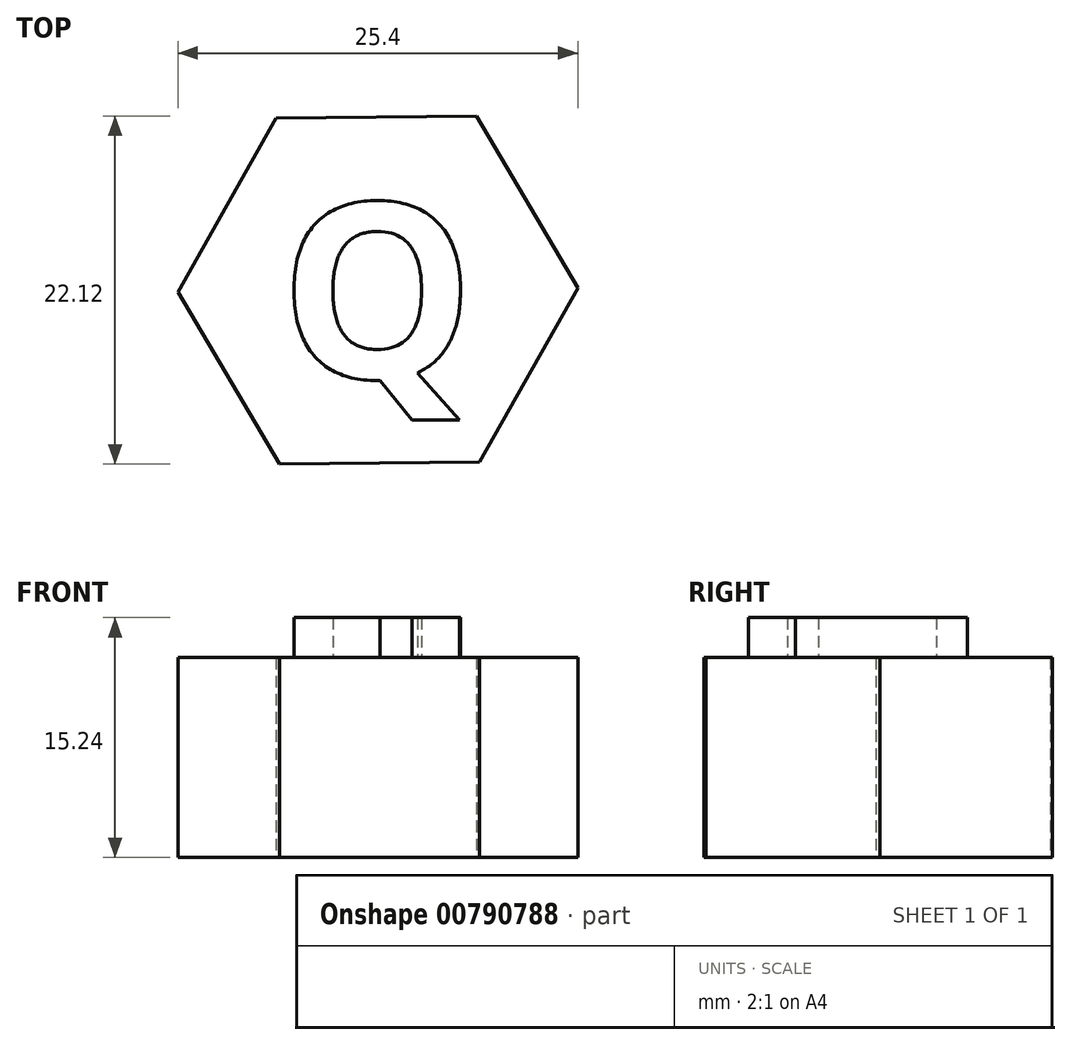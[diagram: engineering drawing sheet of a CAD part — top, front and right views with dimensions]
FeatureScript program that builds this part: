
annotation { "Feature Type Name" : "Feature", "Feature Type Description" : "" }
export const myFeature = defineFeature(function(context is Context, id is Id, definition is map)
    precondition{}
    {
        {
            var Q0;
            Q0=qCreatedBy(makeId("Top.planeOp"),FACE);
            var sketch = newSketch(context, id + "F0", { "sketchPlane" : qUnion([Q0])});
            skCircle(sketch, "E0.cCircle", {"center": v(0, 0) * mm, "radius": 11 * mm, "construction": true});
            skLineSegment(sketch, "E0.0", {"start": v(6.24, 11.06) * mm, "end": v(12.7, 0.13) * mm});
            skLineSegment(sketch, "E0.1", {"start": v(12.7, 0.13) * mm, "end": v(6.46, -10.94) * mm});
            skLineSegment(sketch, "E0.2", {"start": v(6.46, -10.94) * mm, "end": v(-6.24, -11.06) * mm});
            skLineSegment(sketch, "E0.3", {"start": v(-6.24, -11.06) * mm, "end": v(-12.7, -0.13) * mm});
            skLineSegment(sketch, "E0.4", {"start": v(-12.7, -0.13) * mm, "end": v(-6.46, 10.94) * mm});
            skLineSegment(sketch, "E0.5", {"start": v(-6.46, 10.94) * mm, "end": v(6.24, 11.06) * mm});
            skPoint(sketch, "E0.0.midPoint", {"position": v(9.47, 5.6) * mm});
            skSolve(sketch);
        }
        {
            var Q0;
            Q0=qSketchRegion(id+"F0",true);
            extrude(context, id + "F1", {"entities" : qUnion([Q0]), "depth" : 12.7 * mm, "offsetDistance" : 25.4 * mm});
        }
        {
            var Q0;
            Q0=makeQuery(id+"F1.opExtrude","CAP_FACE",FACE,{"disambiguationData":[OSD([sQuery(id+"F0.wireOp",EDGE,"E0.0"),sQuery(id+"F0.wireOp",EDGE,"E0.1"),sQuery(id+"F0.wireOp",EDGE,"E0.2"),sQuery(id+"F0.wireOp",EDGE,"E0.3"),sQuery(id+"F0.wireOp",EDGE,"E0.4"),sQuery(id+"F0.wireOp",EDGE,"E0.5")])],"isStart":false});
            var sketch = newSketch(context, id + "F2", { "sketchPlane" : qUnion([Q0])});
            skText(sketch, "E1", { "text": "Q", "fontName": "OpenSans-Bold.ttf"});
            const initialGuessF2  = {"E1": [-0.00624, -0.0056, 1, 0, 0.0112]};
            skSetInitialGuess(sketch, initialGuessF2);
            skSolve(sketch);
        }
        {
            var Q0;
            Q0 = qSketchRegion(id + "F2", true);
            extrude(context, id + "F3", {"entities" : qUnion([Q0]), "operationType" : NewBodyOperationType.ADD, "depth" : 2.54 * mm, "offsetDistance" : 25.4 * mm});
        }
    });
